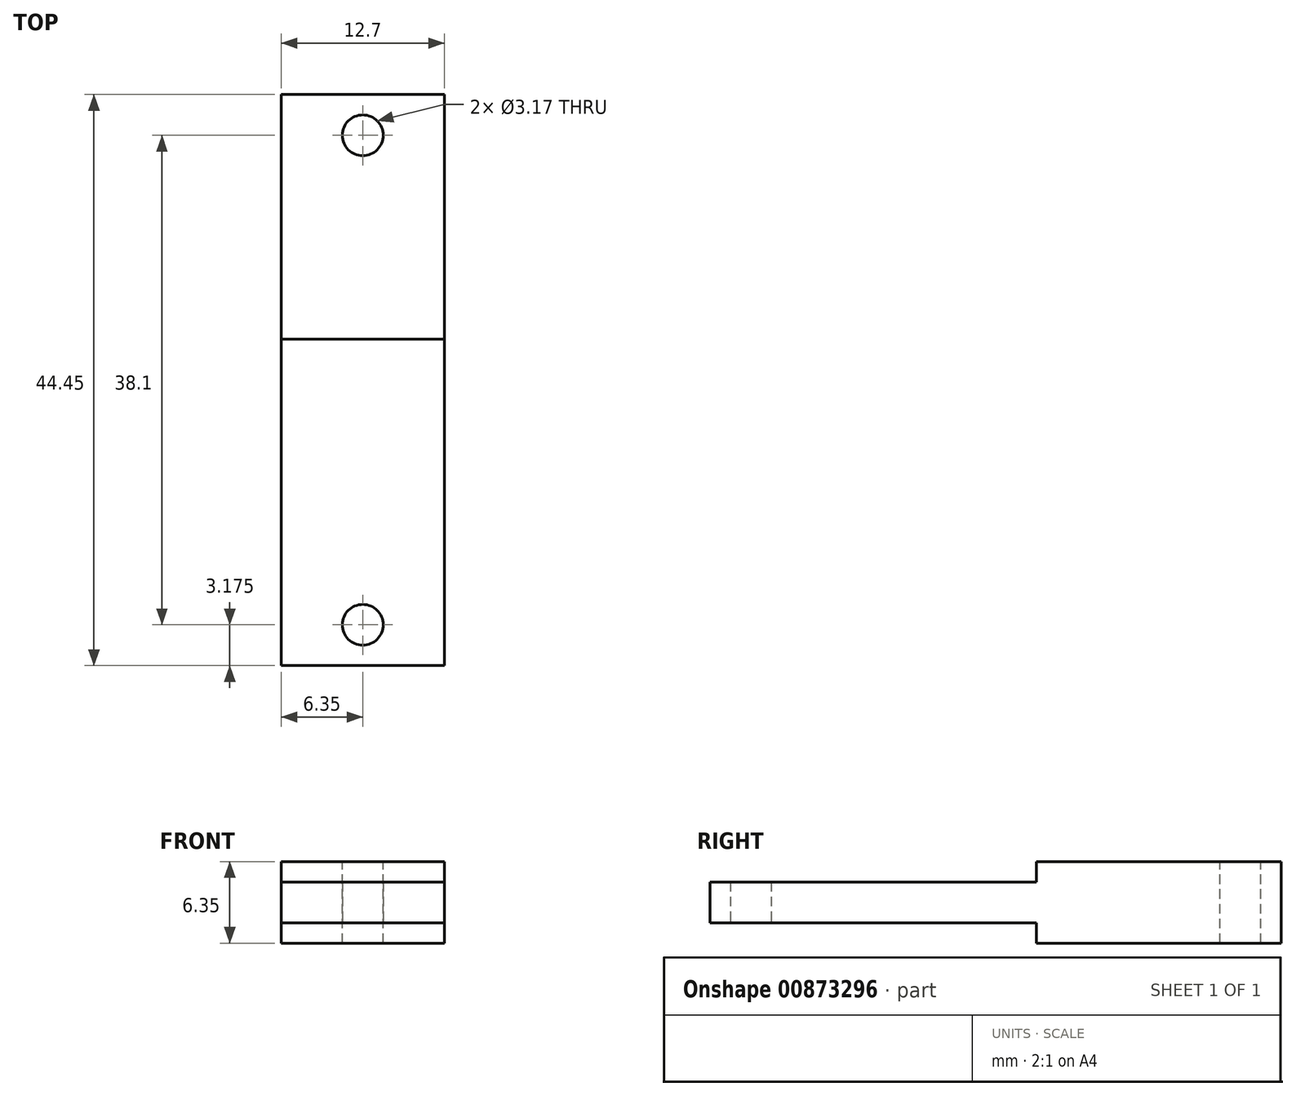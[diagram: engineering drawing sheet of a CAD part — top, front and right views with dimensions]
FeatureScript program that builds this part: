
annotation { "Feature Type Name" : "Feature", "Feature Type Description" : "" }
export const myFeature = defineFeature(function(context is Context, id is Id, definition is map)
    precondition{}
    {
        {
            var Q0;
            Q0=qCreatedBy(makeId("Front.planeOp"),FACE);
            var sketch = newSketch(context, id + "F0", { "sketchPlane" : qUnion([Q0])});
            skLineSegment(sketch, "E0.bottom", {"start": v(0, 0) * mm, "end": v(12.7, 0) * mm});
            skLineSegment(sketch, "E0.top", {"start": v(0, 6.35) * mm, "end": v(12.7, 6.35) * mm});
            skLineSegment(sketch, "E0.left", {"start": v(0, 0) * mm, "end": v(0, 6.35) * mm});
            skLineSegment(sketch, "E0.right", {"start": v(12.7, 0) * mm, "end": v(12.7, 6.35) * mm});
            skSolve(sketch);
        }
        {
            var Q0;
            Q0=makeQuery(id+"F0.imprint","IMPRINT",FACE,{"disambiguationData":[TD([[makeQuery(id+"F0.imprint","IMPRINT",EDGE,{"derivedFrom":sQuery(id+"F0.wireOp",EDGE,"E0.bottom")}),1.0]])]});
            extrude(context, id + "F1", {"entities" : qUnion([Q0]), "oppositeDirection" : true, "depth" : 44.45 * mm, "offsetDistance" : 25.4 * mm});
        }
        {
            var Q0;
            Q0=qCreatedBy(makeId("Front.planeOp"),FACE);
            var sketch = newSketch(context, id + "F2", { "sketchPlane" : qUnion([Q0])});
            skLineSegment(sketch, "E1", {"start": v(-3.81, 4.76) * mm, "end": v(13.97, 4.76) * mm});
            skLineSegment(sketch, "E2", {"start": v(-3.81, 1.59) * mm, "end": v(13.97, 1.59) * mm});
            skLineSegment(sketch, "E3.top", {"start": v(-3.81, 18.77) * mm, "end": v(13.97, 18.77) * mm});
            skLineSegment(sketch, "E3.left", {"start": v(-3.81, 4.76) * mm, "end": v(-3.81, 18.77) * mm});
            skLineSegment(sketch, "E3.right", {"start": v(13.97, 4.76) * mm, "end": v(13.97, 18.77) * mm});
            skLineSegment(sketch, "E4.top", {"start": v(-3.81, -5.59) * mm, "end": v(13.97, -5.59) * mm});
            skLineSegment(sketch, "E4.left", {"start": v(-3.81, 1.59) * mm, "end": v(-3.81, -5.59) * mm});
            skLineSegment(sketch, "E4.right", {"start": v(13.97, 1.59) * mm, "end": v(13.97, -5.59) * mm});
            skSolve(sketch);
        }
        {
            var Q0;
            Q0=makeQuery(id+"F2.imprint","IMPRINT",FACE,{"disambiguationData":[TD([[makeQuery(id+"F2.imprint","IMPRINT",EDGE,{"derivedFrom":sQuery(id+"F2.wireOp",EDGE,"E2")}),-1.0]])]});
            extrude(context, id + "F3", {"entities" : qUnion([Q0]), "operationType" : NewBodyOperationType.REMOVE, "oppositeDirection" : true, "depth" : 6.35 * mm, "offsetDistance" : 25.4 * mm});
        }
        {
            var Q0;
            Q0 = qSketchRegion(id + "F2", true);
            extrude(context, id + "F4", {"entities" : qUnion([Q0]), "operationType" : NewBodyOperationType.REMOVE, "oppositeDirection" : true, "depth" : 25.4 * mm, "offsetDistance" : 25.4 * mm});
        }
        {
            var Q0;
            {var subQ0=sQuery(id+"F2.wireOp",EDGE,"E2");Q0=makeQuery(id+"F4.boolean.opBoolean","MERGE",FACE,{"derivedFrom":[makeQuery(id+"F3.boolean.opBoolean","COPY",FACE,{"derivedFrom":makeQuery(id+"F3.opExtrude","SWEPT_FACE",FACE,{"disambiguationData":[OSD([subQ0])]})})],"fromTools":[makeQuery(id+"F4.opExtrude","SWEPT_FACE",FACE,{"disambiguationData":[OSD([subQ0])]})]});}
            var sketch = newSketch(context, id + "F5", { "sketchPlane" : qUnion([Q0])});
            skCircle(sketch, "E5", {"center": v(6.35, -3.18) * mm, "radius": 1.59 * mm});
            skPoint(sketch, "E5.centerSnap0", {"position": v(6.35, 0) * mm});
            skSolve(sketch);
        }
        {
            var Q0;
            Q0=makeQuery(id+"F5.imprint","IMPRINT",FACE,{"disambiguationData":[TD([[makeQuery(id+"F5.imprint","IMPRINT",EDGE,{"derivedFrom":sQuery(id+"F5.wireOp",EDGE,"E5")}),1.0]])]});
            extrude(context, id + "F6", {"entities" : qUnion([Q0]), "operationType" : NewBodyOperationType.REMOVE, "endBound" : BoundingType.UP_TO_NEXT, "oppositeDirection" : true, "depth" : 25.4 * mm, "offsetDistance" : 25.4 * mm});
        }
        {
            var Q0;
            Q0=makeQuery(id+"F1.opExtrude","SWEPT_FACE",FACE,{"disambiguationData":[OSD([sQuery(id+"F0.wireOp",EDGE,"E0.top")])]});
            var sketch = newSketch(context, id + "F7", { "sketchPlane" : qUnion([Q0])});
            skCircle(sketch, "E6", {"center": v(6.35, 41.28) * mm, "radius": 1.59 * mm});
            skPoint(sketch, "E6.centerSnap0", {"position": v(6.35, 44.45) * mm});
            skSolve(sketch);
        }
        {
            var Q0;
            Q0=makeQuery(id+"F7.imprint","IMPRINT",FACE,{"disambiguationData":[TD([[makeQuery(id+"F7.imprint","IMPRINT",EDGE,{"derivedFrom":sQuery(id+"F7.wireOp",EDGE,"E6")}),1.0]])]});
            var Q1;
            Q1=sQuery(id+"F7.wireOp",EDGE,"E6");
            extrude(context, id + "F8", {"entities" : qUnion([Q0]), "operationType" : NewBodyOperationType.REMOVE, "surfaceEntities" : qUnion([Q1]), "endBound" : BoundingType.UP_TO_NEXT, "oppositeDirection" : true, "depth" : 25.4 * mm, "offsetDistance" : 25.4 * mm});
        }
    });
